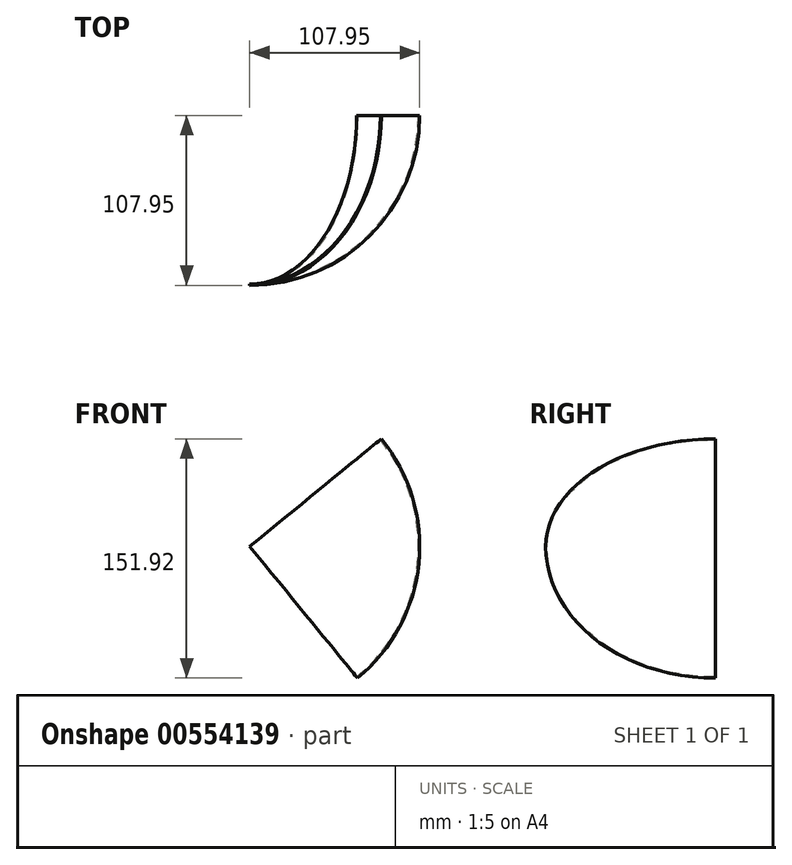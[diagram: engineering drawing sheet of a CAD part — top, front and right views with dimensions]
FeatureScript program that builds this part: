
annotation { "Feature Type Name" : "Feature", "Feature Type Description" : "" }
export const myFeature = defineFeature(function(context is Context, id is Id, definition is map)
    precondition{}
    {
        {
            var Q0;
            Q0=qCreatedBy(makeId("Front.planeOp"),FACE);
            var sketch = newSketch(context, id + "F0", { "sketchPlane" : qUnion([Q0])});
            skArc(sketch, "E0", {"start": v(68.4, -83.52) * mm, "mid": v(107.42, -10.7) * mm, "end": v(83.52, 68.4) * mm});
            skLineSegment(sketch, "E1", {"start": v(0, 0) * mm, "end": v(83.52, 68.4) * mm});
            skLineSegment(sketch, "E2", {"start": v(83.52, 68.4) * mm, "end": v(0, 0) * mm});
            skArc(sketch, "E3", {"start": v(67.9, -82.9) * mm, "mid": v(106.63, -10.61) * mm, "end": v(82.9, 67.9) * mm});
            skLineSegment(sketch, "E4", {"start": v(0, 0) * mm, "end": v(67.9, -82.9) * mm});
            skLineSegment(sketch, "E5", {"start": v(67.9, -82.9) * mm, "end": v(68.4, -83.52) * mm});
            skSolve(sketch);
        }
        {
            var Q0;
            {var subQ0=sQuery(id+"F0.wireOp",EDGE,"E0");Q0=makeQuery(id+"F0.imprint","IMPRINT",FACE,{"disambiguationData":[TD([[makeQuery(id+"F0.imprint","IMPRINT",EDGE,{"derivedFrom":subQ0}),1.0]])]});}
            var Q1;
            Q1=sQuery(id+"F0.wireOp",EDGE,"E4");
            revolve(context, id + "F1", {"entities" : qUnion([Q0]), "axis" : qUnion([Q1]), "revolveType" : RevolveType.ONE_DIRECTION, "angle" : 90 * degree});
        }
    });
